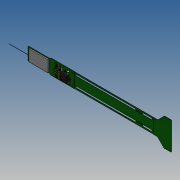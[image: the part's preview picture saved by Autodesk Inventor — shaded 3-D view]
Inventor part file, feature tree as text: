
AUTODESK INVENTOR PART (.ipt)
format: ipt  version: 2018.3 (Build 223284000, 284)  size: 3,019,776 bytes
history: native  units: in
note: dims shown in document units (in); Inventor stores cm internally (conversion verified against a paired STEP export)
features: other x69, extrude x2
ambient origin geometry x8: Origin, YZ Plane, XZ Plane, XY Plane, X Axis, Y Axis, Z Axis, Center Point
bodies: Solid1 (feature_tree), Solid2 (feature_tree), Solid3 (feature_tree), Solid4 (feature_tree), Solid5 (feature_tree), Solid6 (feature_tree), Solid7 (feature_tree), Solid8 (feature_tree), Solid9 (feature_tree), Solid10 (feature_tree), Solid11 (feature_tree), Solid12 (feature_tree), Solid13 (feature_tree), Solid14 (feature_tree), Solid15 (feature_tree), Solid16 (feature_tree), Solid17 (feature_tree), Solid18 (feature_tree), Solid19 (feature_tree), Solid20 (feature_tree), Solid21 (feature_tree), Solid22 (feature_tree), Solid23 (feature_tree), Solid24 (feature_tree), Solid25 (feature_tree), Solid26 (feature_tree), Solid27 (feature_tree), Solid28 (feature_tree), Solid29 (feature_tree), Solid30 (feature_tree), Solid31 (feature_tree), Solid32 (feature_tree), Solid33 (feature_tree), Solid34 (feature_tree), Solid35 (feature_tree), Solid36 (feature_tree), Solid37 (feature_tree), Solid38 (feature_tree), Solid39 (feature_tree), Solid40 (feature_tree), Solid41 (feature_tree), Solid42 (feature_tree), Solid43 (feature_tree), Solid44 (feature_tree), Solid45 (feature_tree), Solid46 (feature_tree), Solid47 (feature_tree), Solid48 (feature_tree), Solid49 (feature_tree), Solid50 (feature_tree), Solid51 (feature_tree), Solid52 (feature_tree), Solid53 (feature_tree), Solid54 (feature_tree), Solid55 (feature_tree), Solid56 (feature_tree), Solid57 (feature_tree), Solid58 (feature_tree), Solid59 (feature_tree), Solid60 (feature_tree), Solid61 (feature_tree), Solid62 (feature_tree), Solid63 (feature_tree), Solid64 (feature_tree), Solid65 (feature_tree), Solid66 (feature_tree), Solid67 (feature_tree), Solid68 (feature_tree), Solid69 (feature_tree), Solid70 (feature_tree), Solid71 (feature_tree)
feature tree (71):
  other  "Board_1:1"
  other  "asic_2:1"
  other  "CerCap_0402_4:1"
  other  "CerCap_0402_4:2"
  other  "CerCap_0402_4:3"
  other  "CerCap_0201_6:1"
  other  "CerCap_0201_6:2"
  other  "CerCap_0201_6:3"
  other  "CerCap_0402_8:1"
  other  "CerCap_0402_8:2"
  other  "CerCap_0402_8:3"
  other  "Capacitor_0306_10:1"
  other  "CerCap_0603_12:1"
  other  "CerCap_0603_12:2"
  other  "CerCap_0603_12:3"
  other  "CerCap_0201_14:1"
  other  "CerCap_0201_14:2"
  other  "CerCap_0201_14:3"
  other  "CerCap_0402_16:1"
  other  "CerCap_0402_16:2"
  other  "CerCap_0402_16:3"
  other  "CerCap_0201_18:1"
  other  "CerCap_0201_18:2"
  other  "CerCap_0201_18:3"
  other  "CerCap_0402_20:1"
  other  "CerCap_0402_20:2"
  other  "CerCap_0402_20:3"
  other  "CerCap_0201_22:1"
  other  "CerCap_0201_22:2"
  other  "CerCap_0201_22:3"
  other  "CerCap_0402_24:1"
  other  "CerCap_0402_24:2"
  other  "CerCap_0402_24:3"
  other  "CerCap_0201_26:1"
  other  "CerCap_0201_26:2"
  other  "CerCap_0201_26:3"
  other  "CerCap_0201_28:1"
  other  "CerCap_0201_28:2"
  other  "CerCap_0201_28:3"
  other  "CerCap_0402_30:1"
  other  "CerCap_0402_30:2"
  other  "CerCap_0402_30:3"
  other  "CerCap_0402_32:1"
  other  "CerCap_0402_32:2"
  other  "CerCap_0402_32:3"
  other  "CerCap_0402_34:1"
  other  "CerCap_0402_34:2"
  other  "CerCap_0402_34:3"
  other  "CerCap_0402_36:1"
  other  "CerCap_0402_36:2"
  other  "CerCap_0402_36:3"
  other  "CerCap_0201_38:1"
  other  "CerCap_0201_38:2"
  other  "CerCap_0201_38:3"
  other  "Res_0402_40:1"
  other  "Res_0402_40:2"
  other  "Res_0402_40:3"
  other  "CerCap_0201_42:1"
  other  "CerCap_0201_42:2"
  other  "CerCap_0201_42:3"
  other  "SON50P300X300-10T165X238_44:1"
  other  "Sphere_46:1"
  other  "Sphere_46:2"
  other  "Sphere_46:3"
  other  "Sphere_46:4"
  extrude  "Extruded_51:1"  [1 undecoded]
  extrude  "Extruded_53:1"  [1 undecoded]
  other  "CerCap_0201_56:1"
  other  "CerCap_0201_56:2"
  other  "CerCap_0201_56:3"
  other  "Board_1:2"
note: 2 required parameter values undecoded (feature->parameter linkage not recoverable at this tier; creation-order binding heuristic only, values carry confidence <= 0.55)
